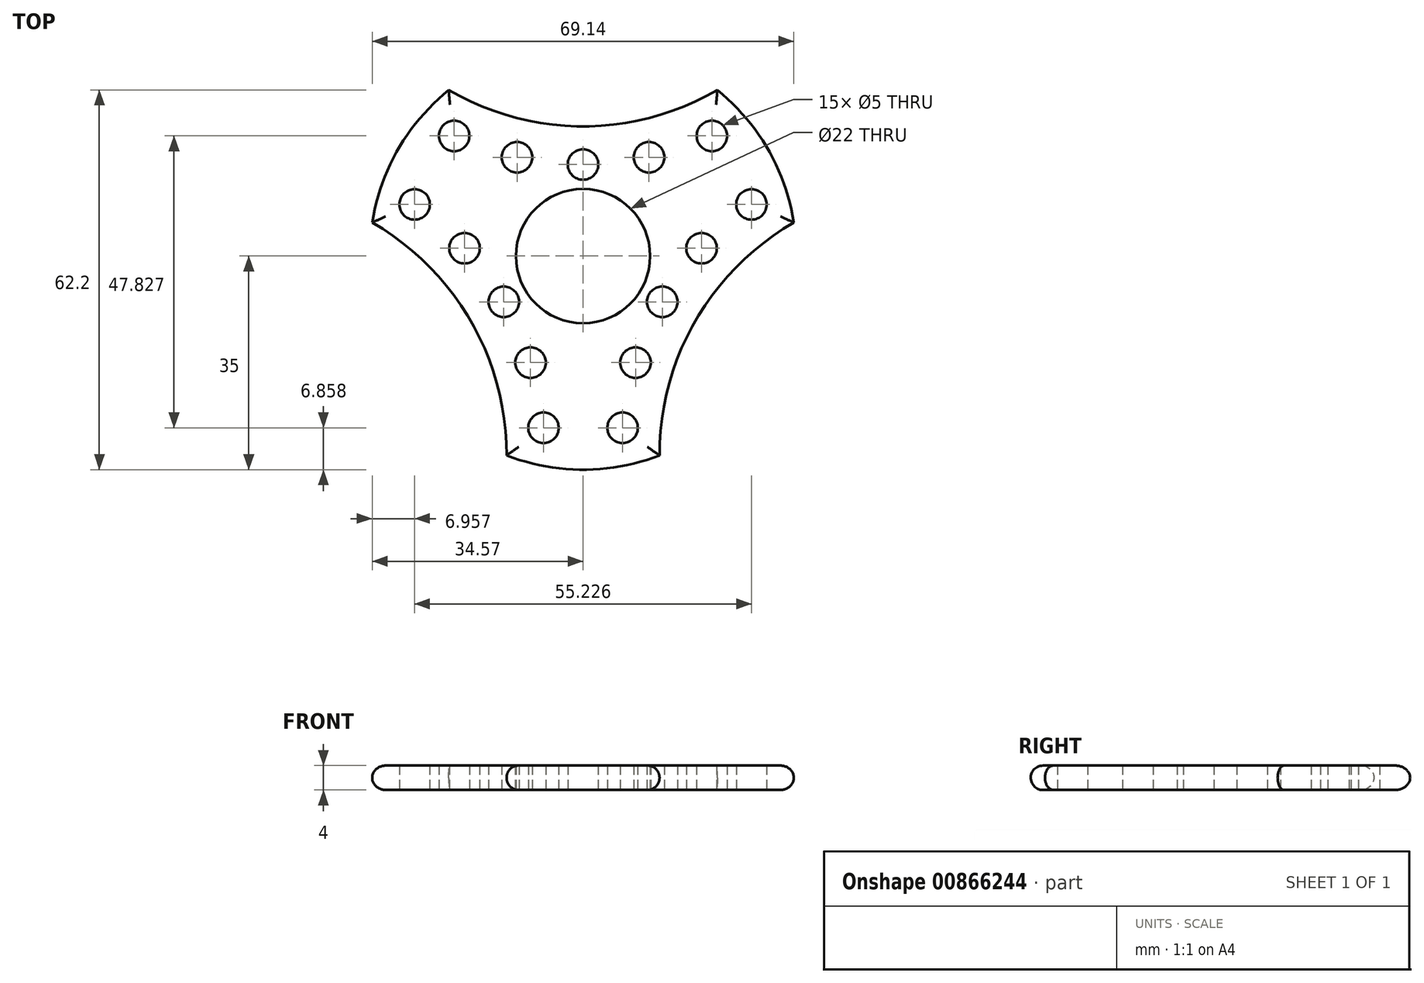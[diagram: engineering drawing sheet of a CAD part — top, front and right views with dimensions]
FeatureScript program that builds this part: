
annotation { "Feature Type Name" : "Feature", "Feature Type Description" : "" }
export const myFeature = defineFeature(function(context is Context, id is Id, definition is map)
    precondition{}
    {
        {
            var Q0;
            Q0=qCreatedBy(makeId("Top.planeOp"),FACE);
            var sketch = newSketch(context, id + "F0", { "sketchPlane" : qUnion([Q0])});
            skCircle(sketch, "E0", {"center": v(0, 0) * mm, "radius": 11 * mm});
            skArc(sketch, "E1", {"start": v(-22.03, 27.2) * mm, "mid": v(0, 21.25) * mm, "end": v(22.03, 27.2) * mm});
            skArc(sketch, "E2", {"start": v(34.57, 5.48) * mm, "mid": v(30.31, 17.5) * mm, "end": v(22.03, 27.2) * mm});
            skArc(sketch, "E3.1.0", {"start": v(-12.54, -32.68) * mm, "mid": v(-18.4, -10.62) * mm, "end": v(-34.57, 5.48) * mm});
            skArc(sketch, "E3.2.0", {"start": v(34.57, 5.48) * mm, "mid": v(18.4, -10.62) * mm, "end": v(12.54, -32.68) * mm});
            skArc(sketch, "E4.trimOffspring", {"start": v(-12.54, -32.68) * mm, "mid": v(0, -35) * mm, "end": v(12.54, -32.68) * mm});
            skArc(sketch, "E5.trimOffspring", {"start": v(-22.03, 27.2) * mm, "mid": v(-30.31, 17.5) * mm, "end": v(-34.57, 5.48) * mm});
            skLineSegment(sketch, "E6", {"start": v(27.61, 8.46) * mm, "end": v(56.3, -32.5) * mm, "construction": true});
            skLineSegment(sketch, "E7", {"start": v(19.43, 1.28) * mm, "end": v(56.3, -32.5) * mm, "construction": true});
            skLineSegment(sketch, "E8", {"start": v(8.6, -17.46) * mm, "end": v(8.6, -17.46) * mm});
            skLineSegment(sketch, "E9", {"start": v(6.48, -28.14) * mm, "end": v(6.48, -28.14) * mm});
            skLineSegment(sketch, "E10", {"start": v(0, 0) * mm, "end": v(56.3, -32.5) * mm, "construction": true});
            skArc(sketch, "E11", {"start": v(27.61, 8.46) * mm, "mid": v(23.32, 5.1) * mm, "end": v(19.43, 1.28) * mm, "construction": true});
            skArc(sketch, "E12", {"start": v(19.43, 1.28) * mm, "mid": v(15.97, -2.93) * mm, "end": v(13, -7.5) * mm, "construction": true});
            skArc(sketch, "E13", {"start": v(13, -7.5) * mm, "mid": v(10.53, -12.36) * mm, "end": v(8.6, -17.46) * mm, "construction": true});
            skLineSegment(sketch, "E14", {"start": v(8.6, -17.46) * mm, "end": v(56.3, -32.5) * mm, "construction": true});
            skLineSegment(sketch, "E15", {"start": v(6.48, -28.14) * mm, "end": v(56.3, -32.5) * mm, "construction": true});
            skArc(sketch, "E16", {"start": v(8.6, -17.46) * mm, "mid": v(7.25, -22.75) * mm, "end": v(6.48, -28.14) * mm, "construction": true});
            skCircle(sketch, "E17", {"center": v(27.61, 8.46) * mm, "radius": 2.5 * mm});
            skCircle(sketch, "E18", {"center": v(19.43, 1.28) * mm, "radius": 2.5 * mm});
            skCircle(sketch, "E19", {"center": v(13, -7.5) * mm, "radius": 2.5 * mm});
            skCircle(sketch, "E20", {"center": v(8.6, -17.46) * mm, "radius": 2.5 * mm});
            skCircle(sketch, "E21", {"center": v(6.48, -28.14) * mm, "radius": 2.5 * mm});
            skCircle(sketch, "E22.1.0", {"center": v(-21.13, 19.68) * mm, "radius": 2.5 * mm});
            skCircle(sketch, "E22.1.1", {"center": v(-10.82, 16.19) * mm, "radius": 2.5 * mm});
            skCircle(sketch, "E22.1.2", {"center": v(0, 15) * mm, "radius": 2.5 * mm});
            skCircle(sketch, "E22.1.3", {"center": v(10.82, 16.19) * mm, "radius": 2.5 * mm});
            skCircle(sketch, "E22.1.4", {"center": v(21.13, 19.68) * mm, "radius": 2.5 * mm});
            skCircle(sketch, "E22.2.0", {"center": v(-6.48, -28.14) * mm, "radius": 2.5 * mm});
            skCircle(sketch, "E22.2.1", {"center": v(-8.6, -17.46) * mm, "radius": 2.5 * mm});
            skCircle(sketch, "E22.2.2", {"center": v(-13, -7.5) * mm, "radius": 2.5 * mm});
            skCircle(sketch, "E22.2.3", {"center": v(-19.43, 1.28) * mm, "radius": 2.5 * mm});
            skCircle(sketch, "E22.2.4", {"center": v(-27.61, 8.46) * mm, "radius": 2.5 * mm});
            skSolve(sketch);
        }
        {
            var Q0;
            Q0=makeQuery(id+"F0.imprint","IMPRINT",FACE,{"disambiguationData":[TD([[makeQuery(id+"F0.imprint","IMPRINT",EDGE,{"derivedFrom":sQuery(id+"F0.wireOp",EDGE,"E0")}),-1.0]])]});
            extrude(context, id + "F1", {"entities" : qUnion([Q0]), "endBound" : BoundingType.SYMMETRIC, "depth" : 4 * mm, "offsetDistance" : 25 * mm});
        }
        {
            var Q0;
            Q0=makeQuery(id+"F1.opExtrude","CAP_EDGE",EDGE,{"disambiguationData":[OSD([sQuery(id+"F0.wireOp",EDGE,"E4.trimOffspring")])],"isStart":false});
            var Q1;
            Q1=makeQuery(id+"F1.opExtrude","CAP_EDGE",EDGE,{"disambiguationData":[OSD([sQuery(id+"F0.wireOp",EDGE,"E3.1.0")])],"isStart":false});
            var Q2;
            Q2=makeQuery(id+"F1.opExtrude","CAP_EDGE",EDGE,{"disambiguationData":[OSD([sQuery(id+"F0.wireOp",EDGE,"E2")])],"isStart":false});
            var Q3;
            Q3=makeQuery(id+"F1.opExtrude","CAP_EDGE",EDGE,{"disambiguationData":[OSD([sQuery(id+"F0.wireOp",EDGE,"E3.1.0")])],"isStart":true});
            var Q4;
            Q4=makeQuery(id+"F1.opExtrude","CAP_EDGE",EDGE,{"disambiguationData":[OSD([sQuery(id+"F0.wireOp",EDGE,"E1")])],"isStart":true});
            var Q5;
            Q5=makeQuery(id+"F1.opExtrude","CAP_EDGE",EDGE,{"disambiguationData":[OSD([sQuery(id+"F0.wireOp",EDGE,"E1")])],"isStart":false});
            var Q6;
            Q6=makeQuery(id+"F1.opExtrude","CAP_EDGE",EDGE,{"disambiguationData":[OSD([sQuery(id+"F0.wireOp",EDGE,"E5.trimOffspring")])],"isStart":true});
            var Q7;
            Q7=makeQuery(id+"F1.opExtrude","CAP_EDGE",EDGE,{"disambiguationData":[OSD([sQuery(id+"F0.wireOp",EDGE,"E5.trimOffspring")])],"isStart":false});
            var Q8;
            Q8=makeQuery(id+"F1.opExtrude","CAP_EDGE",EDGE,{"disambiguationData":[OSD([sQuery(id+"F0.wireOp",EDGE,"E2")])],"isStart":true});
            var Q9;
            Q9=makeQuery(id+"F1.opExtrude","CAP_EDGE",EDGE,{"disambiguationData":[OSD([sQuery(id+"F0.wireOp",EDGE,"E3.2.0")])],"isStart":false});
            var Q10;
            Q10=makeQuery(id+"F1.opExtrude","CAP_EDGE",EDGE,{"disambiguationData":[OSD([sQuery(id+"F0.wireOp",EDGE,"E3.2.0")])],"isStart":true});
            var Q11;
            Q11=makeQuery(id+"F1.opExtrude","CAP_EDGE",EDGE,{"disambiguationData":[OSD([sQuery(id+"F0.wireOp",EDGE,"E4.trimOffspring")])],"isStart":true});
            fillet(context, id + "F2", {"entities" : qUnion([Q0, Q1, Q2, Q3, Q4, Q5, Q6, Q7, Q8, Q9, Q10, Q11]), "radius" : 2 * mm, "tangentPropagation" : true, "allowEdgeOverflow" : false});
        }
    });
